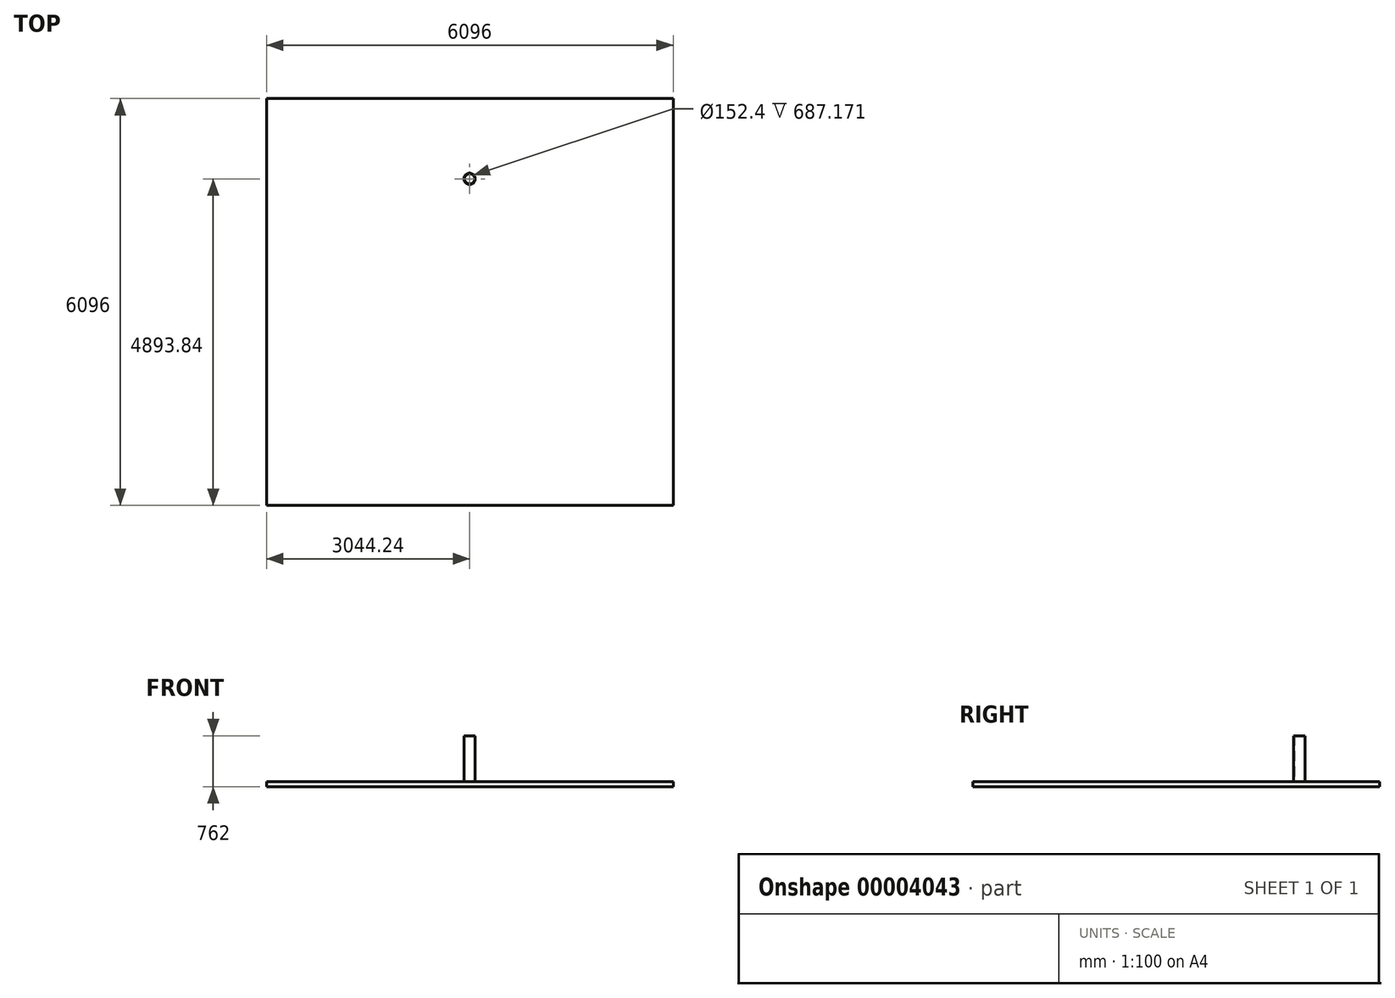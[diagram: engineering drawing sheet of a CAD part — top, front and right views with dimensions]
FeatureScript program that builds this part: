
annotation { "Feature Type Name" : "Feature", "Feature Type Description" : "" }
export const myFeature = defineFeature(function(context is Context, id is Id, definition is map)
    precondition{}
    {
        {
            var Q0;
            Q0=qCreatedBy(makeId("Top.planeOp"),FACE);
            var sketch = newSketch(context, id + "F0", { "sketchPlane" : qUnion([Q0])});
            skCircle(sketch, "E0", {"center": v(0, 0) * mm, "radius": 84.14 * mm});
            skCircle(sketch, "E1", {"center": v(0, 0) * mm, "radius": 76.2 * mm});
            skSolve(sketch);
        }
        {
            var Q0;
            Q0 = qSketchRegion(id + "F0", true);
            extrude(context, id + "F1", {"entities" : qUnion([Q0]), "depth" : 762 * mm});
        }
        {
            var Q0;
            Q0=qCreatedBy(makeId("Top.planeOp"),FACE);
            var sketch = newSketch(context, id + "F2", { "sketchPlane" : qUnion([Q0])});
            skLineSegment(sketch, "E2.bottom", {"start": v(-3044.24, 1202.16) * mm, "end": v(3051.76, 1202.16) * mm});
            skLineSegment(sketch, "E2.top", {"start": v(-3044.24, -4893.84) * mm, "end": v(3051.76, -4893.84) * mm});
            skLineSegment(sketch, "E2.left", {"start": v(-3044.24, 1202.16) * mm, "end": v(-3044.24, -4893.84) * mm});
            skLineSegment(sketch, "E2.right", {"start": v(3051.76, 1202.16) * mm, "end": v(3051.76, -4893.84) * mm});
            skSolve(sketch);
        }
        {
            var Q0;
            Q0 = qSketchRegion(id + "F2", true);
            extrude(context, id + "F3", {"entities" : qUnion([Q0]), "operationType" : NewBodyOperationType.ADD, "depth" : 74.83 * mm});
        }
    });
